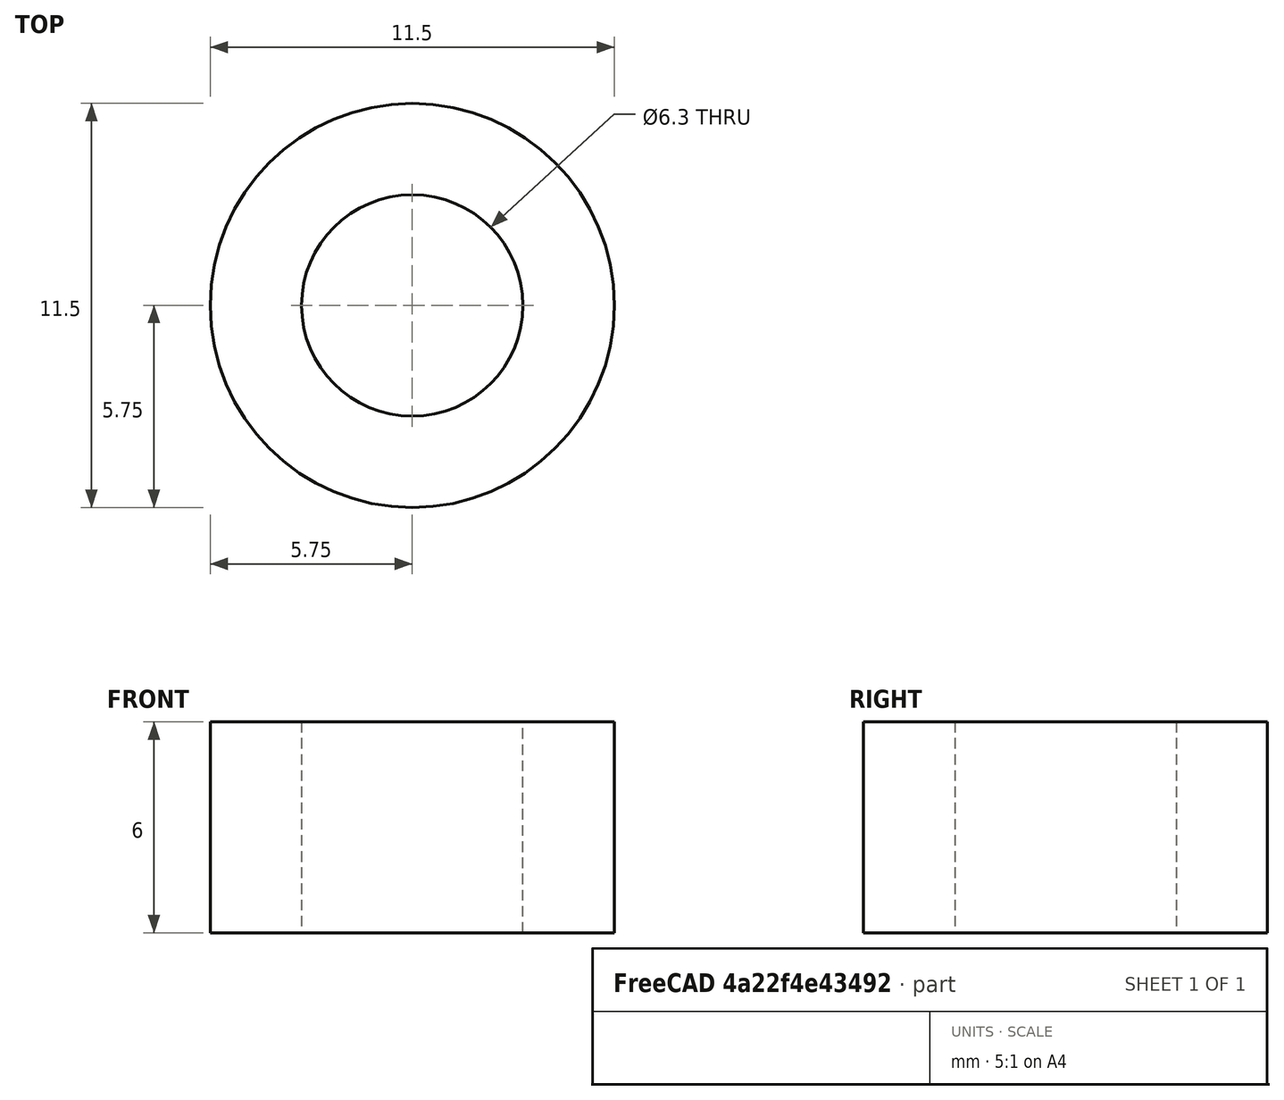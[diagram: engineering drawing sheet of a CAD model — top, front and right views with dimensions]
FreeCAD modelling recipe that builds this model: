
FCSTD DOCUMENT  (FreeCAD 0.21R33668 +26 (Git))
Label: cover_wheel_12-6
License: All rights reserved
LicenseURL: https://en.wikipedia.org/wiki/All_rights_reserved
objects: Sketcher::SketchObject×1, PartDesign::Pad×1, PartDesign::Body×1
note: 4 computed .brp shape members not serialized (recipe doc carries the construction recipe); baked Part::Feature solids carry a one-line shape summary decoded from their .brp

FEATURE [Sketcher::SketchObject] Sketch
  FullyConstrained = true
  MapMode = 5
  Support = -> [XY_Plane]
  sketch-geometry (2):
    g0: Circle CenterX=0 CenterY=0 CenterZ=0 NormalX=0 NormalY=0 NormalZ=1 AngleXU=0 Radius=5.75
    g1: Circle CenterX=0 CenterY=0 CenterZ=0 NormalX=0 NormalY=0 NormalZ=1 AngleXU=0 Radius=3.15
  constraints (4):
    c: Coincident(g0,g-1)
    c: Diameter(g0) = 11.5
    c: Coincident(g1,g0)
    c: Diameter(g1) = 6.3
FEATURE [PartDesign::Pad] Pad
  Direction = (0,0,1)
  Length = 6
  Length2 = 10
  Profile = -> Sketch
  ReferenceAxis = -> Sketch [N_Axis]
  Type = 0
FEATURE [PartDesign::Body] Body
  Group = -> [Sketch,Pad]
  Origin = -> Origin
  Tip = -> Pad
